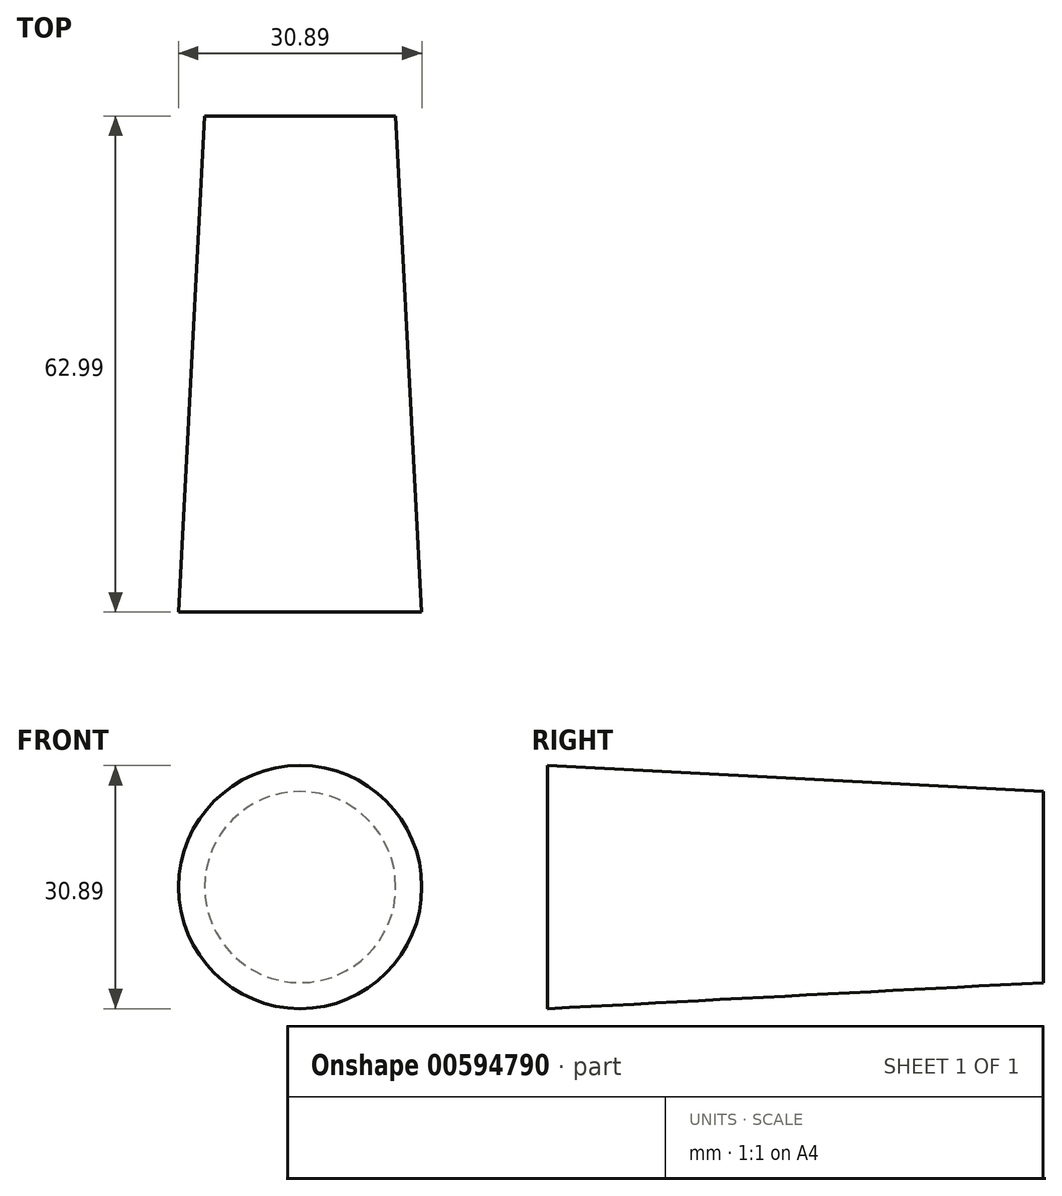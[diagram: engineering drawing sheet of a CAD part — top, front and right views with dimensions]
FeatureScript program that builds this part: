
annotation { "Feature Type Name" : "Feature", "Feature Type Description" : "" }
export const myFeature = defineFeature(function(context is Context, id is Id, definition is map)
    precondition{}
    {
        {
            var Q0;
            Q0=qCreatedBy(makeId("Front.planeOp"),FACE);
            var sketch = newSketch(context, id + "F0", { "sketchPlane" : qUnion([Q0])});
            skCircle(sketch, "E0", {"center": v(-9.6, 7.43) * mm, "radius": 12.14 * mm});
            skPoint(sketch, "E1", {"position": v(-22.21, -18.88) * mm});
            skPoint(sketch, "E2", {"position": v(-18.03, 11.64) * mm});
            skSolve(sketch);
        }
        {
            var Q0;
            Q0=makeQuery(id+"F0.imprint","IMPRINT",FACE,{"disambiguationData":[TD([[makeQuery(id+"F0.imprint","IMPRINT",EDGE,{"derivedFrom":sQuery(id+"F0.wireOp",EDGE,"E0")}),1.0]])]});
            extrude(context, id + "F1", {"entities" : qUnion([Q0]), "depth" : 63 * mm, "offsetDistance" : 25.4 * mm, "hasDraft" : true, "draftAngle" : 3 * degree});
        }
    });
